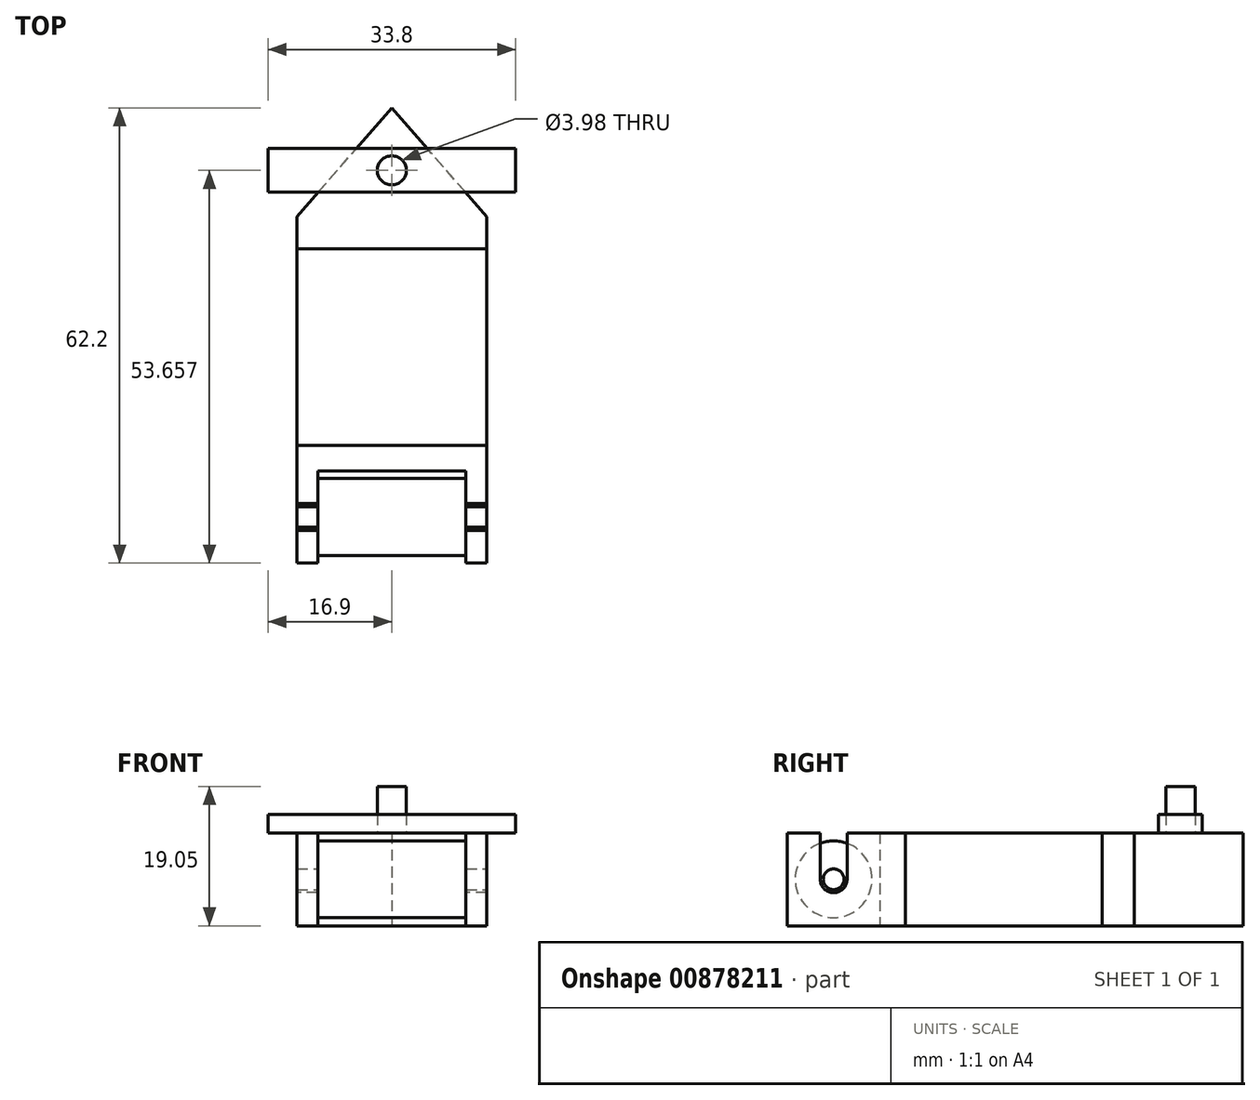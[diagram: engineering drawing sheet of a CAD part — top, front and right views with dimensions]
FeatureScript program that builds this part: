
annotation { "Feature Type Name" : "Feature", "Feature Type Description" : "" }
export const myFeature = defineFeature(function(context is Context, id is Id, definition is map)
    precondition{}
    {
        {
            var Q0;
            Q0=qCreatedBy(makeId("Top.planeOp"),FACE);
            var sketch = newSketch(context, id + "F0", { "sketchPlane" : qUnion([Q0])});
            skLineSegment(sketch, "E0.bottom", {"start": v(0, 21.49) * mm, "end": v(12.97, 21.49) * mm});
            skLineSegment(sketch, "E0.top", {"start": v(0, 0) * mm, "end": v(12.97, 0) * mm});
            skLineSegment(sketch, "E0.left", {"start": v(0, 21.49) * mm, "end": v(0, 0) * mm});
            skLineSegment(sketch, "E0.right", {"start": v(12.97, 21.49) * mm, "end": v(12.97, 0) * mm});
            skLineSegment(sketch, "E1.MirrorCS", {"start": v(12.97, -21.49) * mm, "end": v(12.97, 0) * mm});
            skLineSegment(sketch, "E2.MirrorCS", {"start": v(0, -21.49) * mm, "end": v(12.97, -21.49) * mm});
            skLineSegment(sketch, "E3.MirrorCS", {"start": v(0, -21.49) * mm, "end": v(0, 0) * mm});
            skLineSegment(sketch, "E4.MirrorCS", {"start": v(0, 21.49) * mm, "end": v(-12.97, 21.49) * mm});
            skLineSegment(sketch, "E5.MirrorCS", {"start": v(-12.97, 21.49) * mm, "end": v(-12.97, 0) * mm});
            skLineSegment(sketch, "E6.MirrorCS", {"start": v(-12.97, -21.49) * mm, "end": v(-12.97, 0) * mm});
            skLineSegment(sketch, "E7.MirrorCS", {"start": v(0, -21.49) * mm, "end": v(-12.97, -21.49) * mm});
            skLineSegment(sketch, "E8", {"start": v(12.97, 21.49) * mm, "end": v(12.97, 25.83) * mm});
            skLineSegment(sketch, "E9", {"start": v(12.97, 25.83) * mm, "end": v(0, 40.71) * mm});
            skLineSegment(sketch, "E10.MirrorCS", {"start": v(-12.97, 25.83) * mm, "end": v(0, 40.71) * mm});
            skLineSegment(sketch, "E11.MirrorCS", {"start": v(-12.97, 21.49) * mm, "end": v(-12.97, 25.83) * mm});
            skLineSegment(sketch, "E12", {"start": v(0, 40.71) * mm, "end": v(0, 21.49) * mm});
            skCircle(sketch, "E13", {"center": v(0, 32.17) * mm, "radius": 2 * mm});
            skLineSegment(sketch, "E14.bottom", {"start": v(0, 32.17) * mm, "end": v(16.9, 32.17) * mm});
            skLineSegment(sketch, "E14.top", {"start": v(0, 35.16) * mm, "end": v(16.9, 35.16) * mm});
            skLineSegment(sketch, "E14.left", {"start": v(0, 32.17) * mm, "end": v(0, 35.16) * mm});
            skLineSegment(sketch, "E14.right", {"start": v(16.9, 32.17) * mm, "end": v(16.9, 35.16) * mm});
            skLineSegment(sketch, "E15.MirrorCS", {"start": v(0, 29.17) * mm, "end": v(16.9, 29.17) * mm});
            skLineSegment(sketch, "E16.MirrorCS", {"start": v(16.9, 32.17) * mm, "end": v(16.9, 29.17) * mm});
            skLineSegment(sketch, "E17.MirrorCS", {"start": v(0, 35.16) * mm, "end": v(-16.9, 35.16) * mm});
            skLineSegment(sketch, "E18.MirrorCS", {"start": v(-16.9, 32.17) * mm, "end": v(-16.9, 35.16) * mm});
            skLineSegment(sketch, "E19.MirrorCS", {"start": v(-16.9, 32.17) * mm, "end": v(-16.9, 29.17) * mm});
            skLineSegment(sketch, "E20.MirrorCS", {"start": v(0, 29.17) * mm, "end": v(-16.9, 29.17) * mm});
            skLineSegment(sketch, "E21", {"start": v(-12.97, -5.39) * mm, "end": v(12.97, -5.39) * mm});
            skLineSegment(sketch, "E22.bottom", {"start": v(0, -8.87) * mm, "end": v(10.1, -8.87) * mm});
            skLineSegment(sketch, "E22.top", {"start": v(0, -21.49) * mm, "end": v(10.1, -21.49) * mm});
            skLineSegment(sketch, "E22.left", {"start": v(0, -8.87) * mm, "end": v(0, -21.49) * mm});
            skLineSegment(sketch, "E22.right", {"start": v(10.1, -8.87) * mm, "end": v(10.1, -21.49) * mm});
            skLineSegment(sketch, "E23.MirrorCS", {"start": v(0, -8.87) * mm, "end": v(-10.1, -8.87) * mm});
            skLineSegment(sketch, "E24.MirrorCS", {"start": v(-10.1, -8.87) * mm, "end": v(-10.1, -21.49) * mm});
            skSolve(sketch);
        }
        {
            var Q0;
            {var subQ1=sQuery(id+"F0.wireOp",EDGE,"E0.left");Q0=makeQuery(id+"F0.imprint","IMPRINT",FACE,{"disambiguationData":[TD([[makeQuery(id+"F0.imprint","IMPRINT",EDGE,{"derivedFrom":subQ1}),-1.0]])]});}
            var Q1;
            Q1=makeQuery(id+"F0.imprint","IMPRINT",FACE,{"disambiguationData":[TD([[makeQuery(id+"F0.imprint","IMPRINT",EDGE,{"derivedFrom":sQuery(id+"F0.wireOp",EDGE,"E0.bottom")}),-1.0]])]});
            var Q2;
            {var subQ0=sQuery(id+"F0.wireOp",EDGE,"E0.top");Q2=makeQuery(id+"F0.imprint","IMPRINT",FACE,{"disambiguationData":[TD([[makeQuery(id+"F0.imprint","IMPRINT",EDGE,{"derivedFrom":subQ0}),-1.0]])]});}
            extrude(context, id + "F1", {"entities" : qUnion([Q0, Q1, Q2]), "depth" : 12.7 * mm, "offsetDistance" : 25.4 * mm});
        }
        {
            var Q0;
            {var subQ8=sQuery(id+"F0.wireOp",EDGE,"E23.MirrorCS");Q0=makeQuery(id+"F0.imprint","IMPRINT",FACE,{"disambiguationData":[TD([[makeQuery(id+"F0.imprint","IMPRINT",EDGE,{"derivedFrom":subQ8}),-1.0]])]});}
            var Q1;
            {var subQ8=sQuery(id+"F0.wireOp",EDGE,"E22.bottom");Q1=makeQuery(id+"F0.imprint","IMPRINT",FACE,{"disambiguationData":[TD([[makeQuery(id+"F0.imprint","IMPRINT",EDGE,{"derivedFrom":subQ8}),1.0]])]});}
            var Q2;
            Q2=makeQuery(id+"F1.opExtrude","CAP_FACE",FACE,{"disambiguationData":[OSD([sQuery(id+"F0.wireOp",EDGE,"E0.bottom"),sQuery(id+"F0.wireOp",EDGE,"E0.right"),sQuery(id+"F0.wireOp",EDGE,"E1.MirrorCS"),sQuery(id+"F0.wireOp",EDGE,"E4.MirrorCS"),sQuery(id+"F0.wireOp",EDGE,"E5.MirrorCS"),sQuery(id+"F0.wireOp",EDGE,"E6.MirrorCS"),sQuery(id+"F0.wireOp",EDGE,"E21")])],"isStart":false});
            extrude(context, id + "F2", {"entities" : qUnion([Q0, Q1]), "endBound" : BoundingType.UP_TO_SURFACE, "depth" : 25.4 * mm, "endBoundEntityFace" : qUnion([Q2]), "offsetDistance" : 25.4 * mm});
        }
        {
            var Q0;
            {var subQ5=sQuery(id+"F0.wireOp",EDGE,"E4.MirrorCS");Q0=makeQuery(id+"F0.imprint","IMPRINT",FACE,{"disambiguationData":[TD([[makeQuery(id+"F0.imprint","IMPRINT",EDGE,{"derivedFrom":subQ5}),-1.0]])]});}
            var Q1;
            {var subQ1=sQuery(id+"F0.wireOp",EDGE,"E0.bottom");Q1=makeQuery(id+"F0.imprint","IMPRINT",FACE,{"disambiguationData":[TD([[makeQuery(id+"F0.imprint","IMPRINT",EDGE,{"derivedFrom":subQ1}),1.0]])]});}
            var Q2;
            {var subQ0=sQuery(id+"F0.wireOp",EDGE,"E14.bottom");var subQ7=sQuery(id+"F0.wireOp",EDGE,"E9");var subQ9=makeQuery(id+"F0.imprint","INTERSECT",VERTEX,{"derivedFrom":[subQ7,subQ0]});Q2=makeQuery(id+"F0.imprint","IMPRINT",FACE,{"disambiguationData":[TD([[makeQuery(id+"F0.imprint","IMPRINT",EDGE,{"disambiguationData":[TD([[subQ9,1.0]])],"derivedFrom":subQ7}),1.0]])]});}
            var Q3;
            {var subQ5=sQuery(id+"F0.wireOp",EDGE,"E9");var subQ7=sQuery(id+"F0.wireOp",EDGE,"E14.top");var subQ9=makeQuery(id+"F0.imprint","INTERSECT",VERTEX,{"derivedFrom":[subQ5,subQ7]});Q3=makeQuery(id+"F0.imprint","IMPRINT",FACE,{"disambiguationData":[TD([[makeQuery(id+"F0.imprint","IMPRINT",EDGE,{"disambiguationData":[TD([[subQ9,1.0]])],"derivedFrom":subQ5}),1.0]])]});}
            var Q4;
            {var subQ0=sQuery(id+"F0.wireOp",EDGE,"E14.top");var subQ1=sQuery(id+"F0.wireOp",EDGE,"E9");var subQ2=makeQuery(id+"F0.imprint","INTERSECT",VERTEX,{"derivedFrom":[subQ1,subQ0]});Q4=makeQuery(id+"F0.imprint","IMPRINT",FACE,{"disambiguationData":[TD([[makeQuery(id+"F0.imprint","IMPRINT",EDGE,{"disambiguationData":[TD([[subQ2,-1.0]])],"derivedFrom":subQ1}),1.0]])]});}
            var Q5;
            {var subQ4=sQuery(id+"F0.wireOp",EDGE,"E20.MirrorCS");var subQ5=sQuery(id+"F0.wireOp",EDGE,"E10.MirrorCS");var subQ6=makeQuery(id+"F0.imprint","INTERSECT",VERTEX,{"derivedFrom":[subQ5,subQ4]});Q5=makeQuery(id+"F0.imprint","IMPRINT",FACE,{"disambiguationData":[TD([[makeQuery(id+"F0.imprint","IMPRINT",EDGE,{"disambiguationData":[TD([[subQ6,-1.0]])],"derivedFrom":subQ5}),-1.0]])]});}
            var Q6;
            {var subQ0=sQuery(id+"F0.wireOp",EDGE,"E17.MirrorCS");var subQ1=sQuery(id+"F0.wireOp",EDGE,"E10.MirrorCS");var subQ2=makeQuery(id+"F0.imprint","INTERSECT",VERTEX,{"derivedFrom":[subQ1,subQ0]});Q6=makeQuery(id+"F0.imprint","IMPRINT",FACE,{"disambiguationData":[TD([[makeQuery(id+"F0.imprint","IMPRINT",EDGE,{"disambiguationData":[TD([[subQ2,-1.0]])],"derivedFrom":subQ1}),-1.0]])]});}
            var Q7;
            {var subQ0=sQuery(id+"F0.wireOp",EDGE,"E14.bottom");var subQ1=sQuery(id+"F0.wireOp",EDGE,"E12");var subQ2=makeQuery(id+"F0.imprint","INTERSECT",VERTEX,{"derivedFrom":[subQ1,subQ0]});Q7=makeQuery(id+"F0.imprint","IMPRINT",FACE,{"disambiguationData":[TD([[makeQuery(id+"F0.imprint","IMPRINT",EDGE,{"disambiguationData":[TD([[subQ2,-1.0]])],"derivedFrom":subQ1}),1.0]])]});}
            var Q8;
            {var subQ0=sQuery(id+"F0.wireOp",EDGE,"E12");var subQ1=makeQuery(id+"F0.imprint","INTERSECT",VERTEX,{"derivedFrom":[subQ0,sQuery(id+"F0.wireOp",EDGE,"E14.bottom")]});Q8=makeQuery(id+"F0.imprint","IMPRINT",FACE,{"disambiguationData":[TD([[makeQuery(id+"F0.imprint","IMPRINT",EDGE,{"disambiguationData":[TD([[subQ1,-1.0]])],"derivedFrom":subQ0}),-1.0]])]});}
            var Q9;
            {var subQ0=sQuery(id+"F0.wireOp",EDGE,"E13");var subQ1=sQuery(id+"F0.wireOp",EDGE,"E12");var subQ2=makeQuery(id+"F0.imprint","INTERSECT",VERTEX,{"disambiguationData":[OD(0.0)],"derivedFrom":[subQ1,subQ0]});Q9=makeQuery(id+"F0.imprint","IMPRINT",FACE,{"disambiguationData":[TD([[makeQuery(id+"F0.imprint","IMPRINT",EDGE,{"disambiguationData":[TD([[subQ2,-1.0]])],"derivedFrom":subQ1}),1.0]])]});}
            var Q10;
            Q10=makeQuery(id+"F1.opExtrude","CAP_FACE",FACE,{"disambiguationData":[OSD([sQuery(id+"F0.wireOp",EDGE,"E0.bottom"),sQuery(id+"F0.wireOp",EDGE,"E0.right"),sQuery(id+"F0.wireOp",EDGE,"E1.MirrorCS"),sQuery(id+"F0.wireOp",EDGE,"E4.MirrorCS"),sQuery(id+"F0.wireOp",EDGE,"E5.MirrorCS"),sQuery(id+"F0.wireOp",EDGE,"E6.MirrorCS"),sQuery(id+"F0.wireOp",EDGE,"E21")])],"isStart":false});
            extrude(context, id + "F3", {"entities" : qUnion([Q0, Q1, Q2, Q3, Q4, Q5, Q6, Q7, Q8, Q9]), "endBound" : BoundingType.UP_TO_SURFACE, "depth" : 25.4 * mm, "endBoundEntityFace" : qUnion([Q10]), "offsetDistance" : 25.4 * mm});
        }
        {
            var Q0;
            {var subQ0=sQuery(id+"F0.wireOp",EDGE,"E14.bottom");var subQ1=sQuery(id+"F0.wireOp",EDGE,"E12");var subQ2=makeQuery(id+"F0.imprint","INTERSECT",VERTEX,{"derivedFrom":[subQ1,subQ0]});Q0=makeQuery(id+"F0.imprint","IMPRINT",FACE,{"disambiguationData":[TD([[makeQuery(id+"F0.imprint","IMPRINT",EDGE,{"disambiguationData":[TD([[subQ2,-1.0]])],"derivedFrom":subQ1}),1.0]])]});}
            var Q1;
            {var subQ0=sQuery(id+"F0.wireOp",EDGE,"E13");var subQ1=sQuery(id+"F0.wireOp",EDGE,"E12");var subQ2=makeQuery(id+"F0.imprint","INTERSECT",VERTEX,{"disambiguationData":[OD(0.0)],"derivedFrom":[subQ1,subQ0]});Q1=makeQuery(id+"F0.imprint","IMPRINT",FACE,{"disambiguationData":[TD([[makeQuery(id+"F0.imprint","IMPRINT",EDGE,{"disambiguationData":[TD([[subQ2,-1.0]])],"derivedFrom":subQ1}),1.0]])]});}
            var Q2;
            {var subQ0=sQuery(id+"F0.wireOp",EDGE,"E12");var subQ1=makeQuery(id+"F0.imprint","INTERSECT",VERTEX,{"derivedFrom":[subQ0,sQuery(id+"F0.wireOp",EDGE,"E14.bottom")]});Q2=makeQuery(id+"F0.imprint","IMPRINT",FACE,{"disambiguationData":[TD([[makeQuery(id+"F0.imprint","IMPRINT",EDGE,{"disambiguationData":[TD([[subQ1,-1.0]])],"derivedFrom":subQ0}),-1.0]])]});}
            extrude(context, id + "F4", {"entities" : qUnion([Q0, Q1, Q2]), "operationType" : NewBodyOperationType.ADD, "depth" : 19.05 * mm, "offsetDistance" : 25.4 * mm});
        }
        {
            var Q0;
            {var subQ5=sQuery(id+"F0.wireOp",EDGE,"E16.MirrorCS");Q0=makeQuery(id+"F0.imprint","IMPRINT",FACE,{"disambiguationData":[TD([[makeQuery(id+"F0.imprint","IMPRINT",EDGE,{"derivedFrom":subQ5}),-1.0]])]});}
            var Q1;
            {var subQ0=sQuery(id+"F0.wireOp",EDGE,"E14.bottom");var subQ7=sQuery(id+"F0.wireOp",EDGE,"E9");var subQ9=makeQuery(id+"F0.imprint","INTERSECT",VERTEX,{"derivedFrom":[subQ7,subQ0]});Q1=makeQuery(id+"F0.imprint","IMPRINT",FACE,{"disambiguationData":[TD([[makeQuery(id+"F0.imprint","IMPRINT",EDGE,{"disambiguationData":[TD([[subQ9,1.0]])],"derivedFrom":subQ7}),1.0]])]});}
            var Q2;
            {var subQ5=sQuery(id+"F0.wireOp",EDGE,"E14.right");Q2=makeQuery(id+"F0.imprint","IMPRINT",FACE,{"disambiguationData":[TD([[makeQuery(id+"F0.imprint","IMPRINT",EDGE,{"derivedFrom":subQ5}),1.0]])]});}
            var Q3;
            {var subQ5=sQuery(id+"F0.wireOp",EDGE,"E9");var subQ7=sQuery(id+"F0.wireOp",EDGE,"E14.top");var subQ9=makeQuery(id+"F0.imprint","INTERSECT",VERTEX,{"derivedFrom":[subQ5,subQ7]});Q3=makeQuery(id+"F0.imprint","IMPRINT",FACE,{"disambiguationData":[TD([[makeQuery(id+"F0.imprint","IMPRINT",EDGE,{"disambiguationData":[TD([[subQ9,1.0]])],"derivedFrom":subQ5}),1.0]])]});}
            var Q4;
            {var subQ4=sQuery(id+"F0.wireOp",EDGE,"E20.MirrorCS");var subQ5=sQuery(id+"F0.wireOp",EDGE,"E10.MirrorCS");var subQ6=makeQuery(id+"F0.imprint","INTERSECT",VERTEX,{"derivedFrom":[subQ5,subQ4]});Q4=makeQuery(id+"F0.imprint","IMPRINT",FACE,{"disambiguationData":[TD([[makeQuery(id+"F0.imprint","IMPRINT",EDGE,{"disambiguationData":[TD([[subQ6,-1.0]])],"derivedFrom":subQ5}),-1.0]])]});}
            var Q5;
            {var subQ0=sQuery(id+"F0.wireOp",EDGE,"E18.MirrorCS");Q5=makeQuery(id+"F0.imprint","IMPRINT",FACE,{"disambiguationData":[TD([[makeQuery(id+"F0.imprint","IMPRINT",EDGE,{"derivedFrom":subQ0}),-1.0]])]});}
            extrude(context, id + "F5", {"entities" : qUnion([Q0, Q1, Q2, Q3, Q4, Q5]), "depth" : 15.24 * mm, "offsetDistance" : 25.4 * mm, "hasSecondDirection" : true, "secondDirectionOppositeDirection" : false, "secondDirectionDepth" : 12.7 * mm});
        }
        {
            var Q0;
            Q0=makeQuery(id+"F2.opExtrude","SWEPT_FACE",FACE,{"disambiguationData":[OSD([sQuery(id+"F0.wireOp",EDGE,"E22.right")])]});
            var sketch = newSketch(context, id + "F6", { "sketchPlane" : qUnion([Q0])});
            skCircle(sketch, "E25", {"center": v(15.18, 6.35) * mm, "radius": 1.83 * mm});
            skPoint(sketch, "E25.centerSnap0", {"position": v(21.49, 6.35) * mm});
            skPoint(sketch, "E25.centerSnap1", {"position": v(15.18, 12.7) * mm});
            skCircle(sketch, "E26", {"center": v(15.18, 6.35) * mm, "radius": 1.42 * mm});
            skLineSegment(sketch, "E27", {"start": v(13.35, 6.35) * mm, "end": v(13.35, 12.7) * mm});
            skLineSegment(sketch, "E28", {"start": v(17, 6.35) * mm, "end": v(17, 12.7) * mm});
            skCircle(sketch, "E29", {"center": v(15.18, 6.35) * mm, "radius": 5.25 * mm});
            skSolve(sketch);
        }
        {
            var Q0;
            Q0=makeQuery(id+"F6.imprint","IMPRINT",FACE,{"disambiguationData":[TD([[makeQuery(id+"F6.imprint","IMPRINT",EDGE,{"derivedFrom":sQuery(id+"F6.wireOp",EDGE,"E26")}),-1.0]])]});
            var Q1;
            Q1=makeQuery(id+"F6.imprint","IMPRINT",FACE,{"disambiguationData":[TD([[makeQuery(id+"F6.imprint","IMPRINT",EDGE,{"derivedFrom":sQuery(id+"F6.wireOp",EDGE,"E26")}),1.0]])]});
            var Q2;
            {var subQ0=sQuery(id+"F6.wireOp",EDGE,"E27");Q2=makeQuery(id+"F6.imprint","IMPRINT",FACE,{"disambiguationData":[TD([[makeQuery(id+"F6.imprint","IMPRINT",EDGE,{"derivedFrom":subQ0}),-1.0]])]});}
            extrude(context, id + "F7", {"entities" : qUnion([Q0, Q1, Q2]), "operationType" : NewBodyOperationType.REMOVE, "endBound" : BoundingType.THROUGH_ALL, "oppositeDirection" : true, "depth" : 25.4 * mm, "offsetDistance" : 25.4 * mm, "hasSecondDirection" : true, "secondDirectionBound" : SecondDirectionBoundingType.THROUGH_ALL, "secondDirectionOppositeDirection" : false, "secondDirectionDepth" : 25.4 * mm});
        }
        {
            var Q0;
            Q0=makeQuery(id+"F6.imprint","IMPRINT",FACE,{"disambiguationData":[TD([[makeQuery(id+"F6.imprint","IMPRINT",EDGE,{"derivedFrom":sQuery(id+"F6.wireOp",EDGE,"E26")}),1.0]])]});
            var Q1;
            Q1=makeQuery(id+"F2.opExtrude","SWEPT_FACE",FACE,{"disambiguationData":[OSD([sQuery(id+"F0.wireOp",EDGE,"E6.MirrorCS")])]});
            var Q2;
            Q2=makeQuery(id+"F2.opExtrude","SWEPT_FACE",FACE,{"disambiguationData":[OSD([sQuery(id+"F0.wireOp",EDGE,"E1.MirrorCS")])]});
            extrude(context, id + "F8", {"entities" : qUnion([Q0]), "endBound" : BoundingType.UP_TO_SURFACE, "depth" : 25.4 * mm, "endBoundEntityFace" : qUnion([Q1]), "offsetDistance" : 25.4 * mm, "hasSecondDirection" : true, "secondDirectionBound" : SecondDirectionBoundingType.UP_TO_SURFACE, "secondDirectionOppositeDirection" : true, "secondDirectionDepth" : 25.4 * mm, "secondDirectionBoundEntityFace" : qUnion([Q2])});
        }
        {
            var Q0;
            Q0=makeQuery(id+"F6.imprint","IMPRINT",FACE,{"disambiguationData":[TD([[makeQuery(id+"F6.imprint","IMPRINT",EDGE,{"derivedFrom":sQuery(id+"F6.wireOp",EDGE,"E26")}),-1.0]])]});
            var Q1;
            {var subQ0=sQuery(id+"F6.wireOp",EDGE,"E27");var subQ1=sQuery(id+"F6.wireOp",EDGE,"E25");var subQ2=makeQuery(id+"F6.imprint","INTERSECT",VERTEX,{"derivedFrom":[subQ1,subQ0]});Q1=makeQuery(id+"F6.imprint","IMPRINT",FACE,{"disambiguationData":[TD([[makeQuery(id+"F6.imprint","IMPRINT",EDGE,{"disambiguationData":[TD([[subQ2,1.0]])],"derivedFrom":subQ1}),-1.0]])]});}
            var Q2;
            {var subQ0=sQuery(id+"F6.wireOp",EDGE,"E27");var subQ1=sQuery(id+"F6.wireOp",EDGE,"E25");var subQ2=makeQuery(id+"F6.imprint","INTERSECT",VERTEX,{"derivedFrom":[subQ1,subQ0]});Q2=makeQuery(id+"F6.imprint","IMPRINT",FACE,{"disambiguationData":[TD([[makeQuery(id+"F6.imprint","IMPRINT",EDGE,{"disambiguationData":[TD([[subQ2,-1.0]])],"derivedFrom":subQ1}),-1.0]])]});}
            var Q3;
            Q3=makeQuery(id+"F2.opExtrude","SWEPT_FACE",FACE,{"disambiguationData":[OSD([sQuery(id+"F0.wireOp",EDGE,"E24.MirrorCS")])]});
            extrude(context, id + "F9", {"entities" : qUnion([Q0, Q1, Q2]), "operationType" : NewBodyOperationType.ADD, "endBound" : BoundingType.UP_TO_SURFACE, "depth" : 25.4 * mm, "endBoundEntityFace" : qUnion([Q3]), "offsetDistance" : 25.4 * mm});
        }
    });
